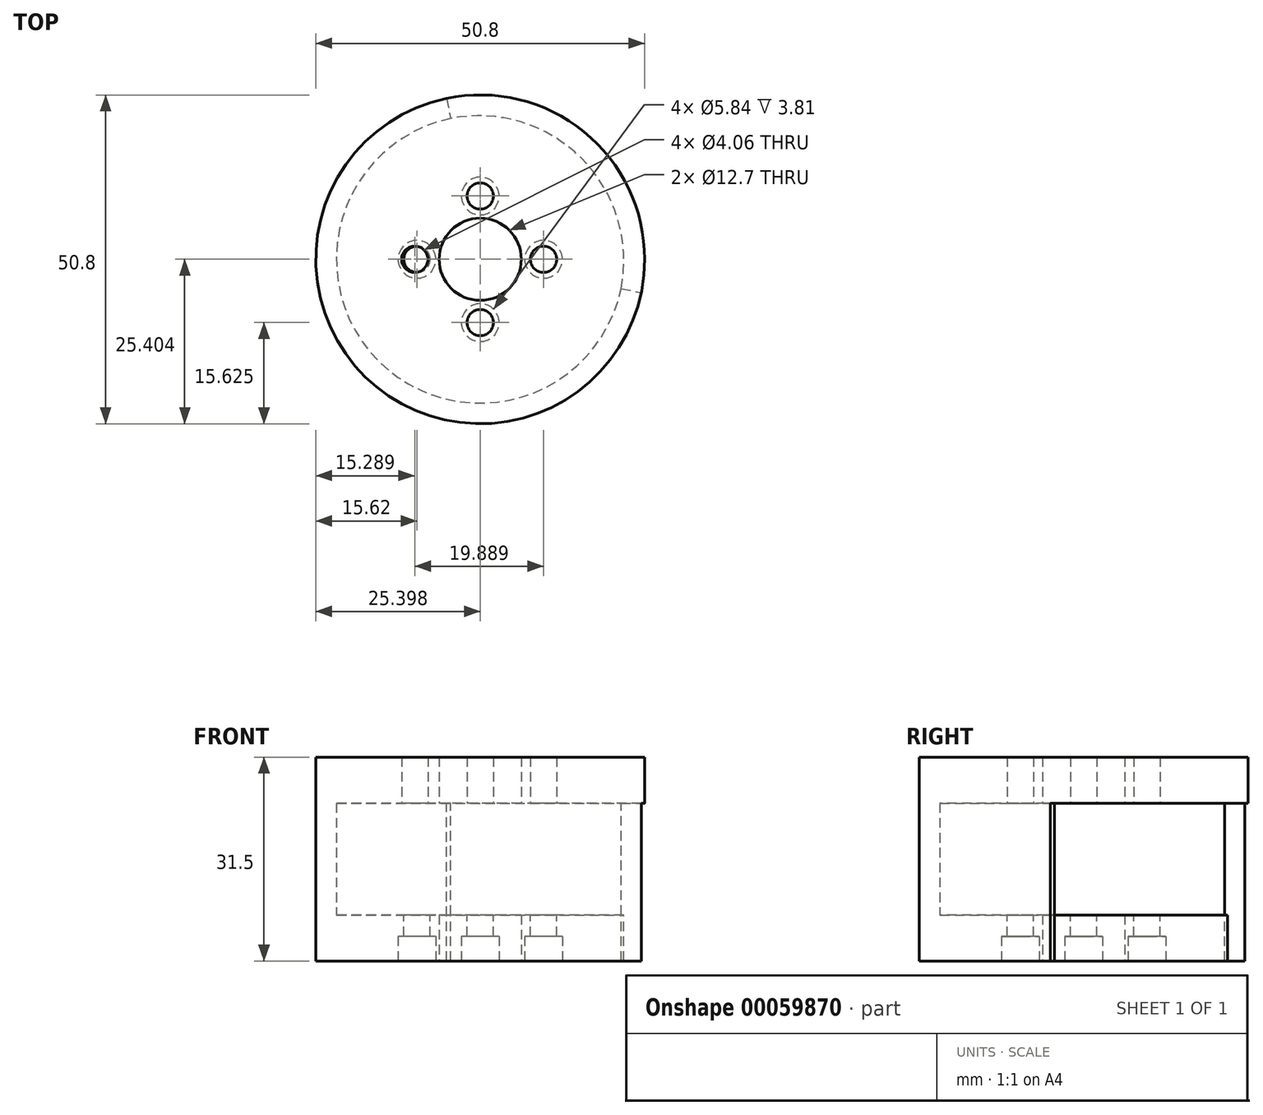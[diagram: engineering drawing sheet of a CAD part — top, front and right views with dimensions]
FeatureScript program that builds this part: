
annotation { "Feature Type Name" : "Feature", "Feature Type Description" : "" }
export const myFeature = defineFeature(function(context is Context, id is Id, definition is map)
    precondition{}
    {
        {
            var Q0;
            Q0=qCreatedBy(makeId("Top.planeOp"),FACE);
            var sketch = newSketch(context, id + "F0", { "sketchPlane" : qUnion([Q0])});
            skCircle(sketch, "E0", {"center": v(-2.91, -0.12) * mm, "radius": 25.4 * mm});
            skCircle(sketch, "E1", {"center": v(-2.91, -0.12) * mm, "radius": 6.35 * mm});
            skCircle(sketch, "E2", {"center": v(-2.91, -0.12) * mm, "radius": 22.23 * mm});
            skSolve(sketch);
        }
        {
            var Q0;
            Q0=makeQuery(id+"F0.imprint","IMPRINT",FACE,{"disambiguationData":[TD([[makeQuery(id+"F0.imprint","IMPRINT",EDGE,{"derivedFrom":sQuery(id+"F0.wireOp",EDGE,"E1")}),-1.0]])]});
            var Q1;
            Q1=makeQuery(id+"F0.imprint","IMPRINT",FACE,{"disambiguationData":[TD([[makeQuery(id+"F0.imprint","IMPRINT",EDGE,{"derivedFrom":sQuery(id+"F0.wireOp",EDGE,"E0")}),1.0]])]});
            extrude(context, id + "F1", {"entities" : qUnion([Q0, Q1]), "depth" : 7.11 * mm});
        }
        {
            var Q0;
            Q0=makeQuery(id+"F1.opExtrude","CAP_FACE",FACE,{"disambiguationData":[OSD([sQuery(id+"F0.wireOp",EDGE,"E0"),sQuery(id+"F0.wireOp",EDGE,"E1")])],"isStart":false});
            var sketch = newSketch(context, id + "F2", { "sketchPlane" : qUnion([Q0])});
            skCircle(sketch, "E3", {"center": v(-2.91, -0.12) * mm, "radius": 22.23 * mm});
            skCircle(sketch, "E4", {"center": v(-2.91, -0.12) * mm, "radius": 25.4 * mm});
            skSolve(sketch);
        }
        {
            var Q0;
            Q0=makeQuery(id+"F2.imprint","IMPRINT",FACE,{"disambiguationData":[TD([[makeQuery(id+"F2.imprint","IMPRINT",EDGE,{"derivedFrom":sQuery(id+"F2.wireOp",EDGE,"E3")}),-1.0]])]});
            extrude(context, id + "F3", {"entities" : qUnion([Q0]), "operationType" : NewBodyOperationType.ADD, "depth" : 17.27 * mm});
        }
        {
            var Q0;
            Q0=makeQuery(id+"F1.opExtrude","CAP_FACE",FACE,{"disambiguationData":[OSD([sQuery(id+"F0.wireOp",EDGE,"E0"),sQuery(id+"F0.wireOp",EDGE,"E1")])],"isStart":false});
            var sketch = newSketch(context, id + "F4", { "sketchPlane" : qUnion([Q0])});
            skCircle(sketch, "E5", {"center": v(-2.91, 9.66) * mm, "radius": 2.03 * mm});
            skCircle(sketch, "E6", {"center": v(-12.7, -0.12) * mm, "radius": 2.03 * mm});
            skCircle(sketch, "E7", {"center": v(-2.91, -9.9) * mm, "radius": 2.03 * mm});
            skCircle(sketch, "E8", {"center": v(6.87, -0.12) * mm, "radius": 2.03 * mm});
            skPoint(sketch, "E9.orphan", {"position": v(-2.91, -0.12) * mm});
            skSolve(sketch);
        }
        {
            var Q0;
            Q0=makeQuery(id+"F4.imprint","IMPRINT",FACE,{"disambiguationData":[TD([[makeQuery(id+"F4.imprint","IMPRINT",EDGE,{"derivedFrom":sQuery(id+"F4.wireOp",EDGE,"E5")}),1.0]])]});
            var Q1;
            Q1=makeQuery(id+"F4.imprint","IMPRINT",FACE,{"disambiguationData":[TD([[makeQuery(id+"F4.imprint","IMPRINT",EDGE,{"derivedFrom":sQuery(id+"F4.wireOp",EDGE,"E6")}),1.0]])]});
            var Q2;
            Q2=makeQuery(id+"F4.imprint","IMPRINT",FACE,{"disambiguationData":[TD([[makeQuery(id+"F4.imprint","IMPRINT",EDGE,{"derivedFrom":sQuery(id+"F4.wireOp",EDGE,"E8")}),1.0]])]});
            var Q3;
            Q3=makeQuery(id+"F4.imprint","IMPRINT",FACE,{"disambiguationData":[TD([[makeQuery(id+"F4.imprint","IMPRINT",EDGE,{"derivedFrom":sQuery(id+"F4.wireOp",EDGE,"E7")}),1.0]])]});
            extrude(context, id + "F5", {"entities" : qUnion([Q0, Q1, Q2, Q3]), "operationType" : NewBodyOperationType.REMOVE, "oppositeDirection" : true, "depth" : 21.3 * mm});
        }
        {
            var Q0;
            Q0=makeQuery(id+"F0.imprint","IMPRINT",FACE,{"disambiguationData":[TD([[makeQuery(id+"F0.imprint","IMPRINT",EDGE,{"derivedFrom":sQuery(id+"F0.wireOp",EDGE,"E1")}),-1.0]])]});
            var sketch = newSketch(context, id + "F6", { "sketchPlane" : qUnion([Q0])});
            skCircle(sketch, "E10", {"center": v(-2.91, -9.9) * mm, "radius": 2.92 * mm});
            skCircle(sketch, "E11", {"center": v(6.87, -0.12) * mm, "radius": 2.92 * mm});
            skCircle(sketch, "E12", {"center": v(-2.91, 9.66) * mm, "radius": 2.92 * mm});
            skCircle(sketch, "E13", {"center": v(-12.7, -0.12) * mm, "radius": 2.92 * mm});
            skPoint(sketch, "E14.orphan", {"position": v(-2.91, -0.12) * mm});
            skSolve(sketch);
        }
        {
            var Q0;
            Q0=qSketchRegion(id+"F6",true);
            extrude(context, id + "F7", {"entities" : qUnion([Q0]), "operationType" : NewBodyOperationType.REMOVE, "depth" : 3.8 * mm});
        }
        {
            var Q0;
            Q0=makeQuery(id+"F3.opExtrude","CAP_FACE",FACE,{"disambiguationData":[OSD([sQuery(id+"F2.wireOp",EDGE,"E3"),sQuery(id+"F2.wireOp",EDGE,"E4")])],"isStart":false});
            var sketch = newSketch(context, id + "F8", { "sketchPlane" : qUnion([Q0])});
            skPoint(sketch, "E15.start.orphan", {"position": v(-2.91, -0.12) * mm});
            skPoint(sketch, "E16.end.orphan", {"position": v(22.58, -0.12) * mm});
            skArc(sketch, "E17", {"start": v(18.85, -4.63) * mm, "mid": v(12.69, 15.52) * mm, "end": v(-7.48, 21.63) * mm});
            skArc(sketch, "E18", {"start": v(21.96, -5.27) * mm, "mid": v(15.07, 17.9) * mm, "end": v(-8.13, 24.74) * mm});
            skLineSegment(sketch, "E19", {"start": v(-8.13, 24.74) * mm, "end": v(-7.48, 21.63) * mm});
            skLineSegment(sketch, "E20", {"start": v(18.85, -4.63) * mm, "end": v(21.96, -5.27) * mm});
            skSolve(sketch);
        }
        {
            var Q0;
            Q0=qSketchRegion(id+"F8",true);
            extrude(context, id + "F9", {"entities" : qUnion([Q0]), "operationType" : NewBodyOperationType.REMOVE, "oppositeDirection" : true, "depth" : 17.27 * mm});
        }
        {
            var Q0;
            Q0=makeQuery(id+"F3.opExtrude","CAP_FACE",FACE,{"disambiguationData":[OSD([sQuery(id+"F2.wireOp",EDGE,"E3"),sQuery(id+"F2.wireOp",EDGE,"E4")])],"isStart":false});
            var sketch = newSketch(context, id + "F10", { "sketchPlane" : qUnion([Q0])});
            skCircle(sketch, "E21", {"center": v(-2.91, -0.12) * mm, "radius": 25.4 * mm});
            skCircle(sketch, "E22", {"center": v(-2.91, -0.12) * mm, "radius": 6.35 * mm});
            skLineSegment(sketch, "E23", {"start": v(-2.91, -0.12) * mm, "end": v(-2.91, 9.66) * mm});
            skLineSegment(sketch, "E24", {"start": v(-2.91, -0.12) * mm, "end": v(-2.91, -9.9) * mm});
            skLineSegment(sketch, "E25", {"start": v(-2.91, -0.12) * mm, "end": v(6.87, -0.12) * mm});
            skLineSegment(sketch, "E26", {"start": v(-2.91, -0.12) * mm, "end": v(-13.02, -0.12) * mm});
            skCircle(sketch, "E27", {"center": v(-13.02, -0.12) * mm, "radius": 2.03 * mm});
            skCircle(sketch, "E28", {"center": v(-2.91, 9.66) * mm, "radius": 2.03 * mm});
            skCircle(sketch, "E29", {"center": v(6.87, -0.12) * mm, "radius": 2.03 * mm});
            skCircle(sketch, "E30", {"center": v(-2.91, -9.9) * mm, "radius": 2.03 * mm});
            skSolve(sketch);
        }
        {
            var Q0;
            Q0 = qSketchRegion(id + "F10", true);
            extrude(context, id + "F11", {"entities" : qUnion([Q0]), "operationType" : NewBodyOperationType.ADD, "depth" : 7.11 * mm});
        }
        {
            var Q0;
            Q0 = qSketchRegion(id + "F8", true);
            extrude(context, id + "F12", {"entities" : qUnion([Q0]), "operationType" : NewBodyOperationType.REMOVE, "oppositeDirection" : true, "depth" : 25.4 * mm});
        }
    });
